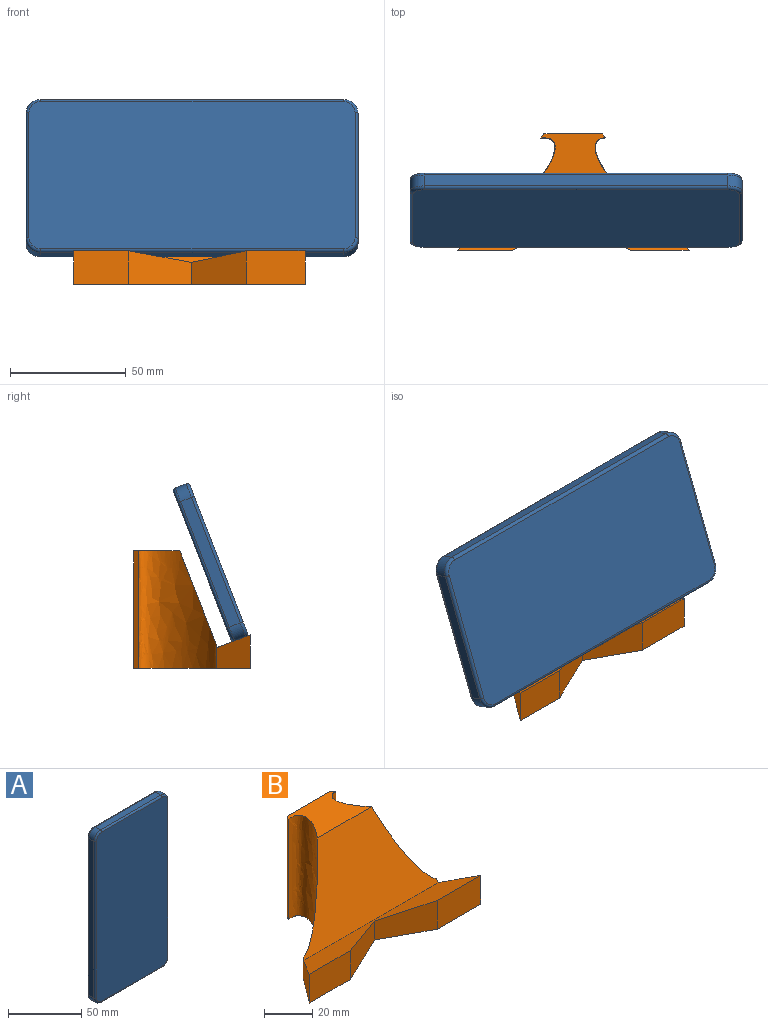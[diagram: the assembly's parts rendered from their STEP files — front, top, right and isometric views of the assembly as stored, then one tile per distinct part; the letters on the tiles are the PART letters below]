
ASSEMBLY  parts=2 mates=1
PART A: 26 faces, bbox 71.9x7.6x144.6 mm
  f0: plane 58.17x5.08mm, normal (0,0,-1), area 295.5mm2, adj f1,f7,f14,f22
  f1: cylinder r=6.35mm len=6.35mm, axis (0,1,0), area 50.7mm2, adj f0,f2,f12,f20
  f2: plane 130.81x5.08mm, normal (1,0,0), area 664.5mm2, adj f1,f3,f10,f18
  f3: cylinder r=6.35mm len=6.35mm, axis (0,1,0), area 50.7mm2, adj f2,f4,f11,f19
  f4: plane 58.17x5.08mm, normal (0,0,1), area 295.5mm2, adj f3,f5,f13,f21
  f5: cylinder r=6.35mm len=6.35mm, axis (0,1,0), area 50.7mm2, adj f4,f6,f15,f23
  f6: plane 130.81x5.08mm, normal (-1,0,0), area 664.5mm2, adj f5,f7,f17,f25
  f7: cylinder r=6.35mm len=6.35mm, axis (0,1,0), area 50.7mm2, adj f0,f6,f16,f24
  f8: plane 140.97x68.33mm, normal (0,-1,0), area 9609.8mm2, adj f18,f19,f20,f21,f22,f23,f24,f25
  f9: plane 140.97x68.33mm, normal (0,1,0), area 9609.8mm2, adj f10,f11,f12,f13,f14,f15,f16,f17
  f10: cylinder r=1.27mm len=130.81mm, axis (0,0,1), area 261mm2, adj f2,f9,f11,f12
  f11: torus R=5.08mm, axis (0,-1,0), area 18.5mm2, adj f3,f9,f10,f13
  f12: torus R=5.08mm, axis (0,-1,0), area 18.5mm2, adj f1,f9,f10,f14
  f13: cylinder r=1.27mm len=58.17mm, axis (-1,0,0), area 116mm2, adj f4,f9,f11,f15
  f14: cylinder r=1.27mm len=58.17mm, axis (1,0,0), area 116mm2, adj f0,f9,f12,f16
  f15: torus R=5.08mm, axis (0,-1,0), area 18.5mm2, adj f5,f9,f13,f17
  f16: torus R=5.08mm, axis (0,-1,0), area 18.5mm2, adj f7,f9,f14,f17
  f17: cylinder r=1.27mm len=130.81mm, axis (0,0,-1), area 261mm2, adj f6,f9,f15,f16
  f18: cylinder r=1.27mm len=130.81mm, axis (0,0,-1), area 261mm2, adj f2,f8,f19,f20
  f19: torus R=5.08mm, axis (0,-1,0), area 18.5mm2, adj f3,f8,f18,f21
  f20: torus R=5.08mm, axis (0,-1,0), area 18.5mm2, adj f1,f8,f18,f22
  f21: cylinder r=1.27mm len=58.17mm, axis (1,0,0), area 116mm2, adj f4,f8,f19,f23
  f22: cylinder r=1.27mm len=58.17mm, axis (-1,0,0), area 116mm2, adj f0,f8,f20,f24
  f23: torus R=5.08mm, axis (0,-1,0), area 18.5mm2, adj f5,f8,f21,f25
  f24: torus R=5.08mm, axis (0,-1,0), area 18.5mm2, adj f7,f8,f22,f25
  f25: cylinder r=1.27mm len=130.81mm, axis (0,0,1), area 261mm2, adj f6,f8,f23,f24
PART B: 15 faces, bbox 100.1x50.2x50.8 mm
  f0: plane 50.8x1.83mm, normal (-0.8,0.6,0), area 116mm2, adj f4,f10,f11,f14
  f1: plane 14.57x14.53mm, normal (-0.8,0.6,0), area 212.8mm2, adj f4,f5,f6,f12,f14
  f2: plane 14.84x14.57mm, normal (0.8,0.6,0), area 216.9mm2, adj f4,f5,f7,f12,f13
  f3: plane 50.8x1.73mm, normal (0.8,0.6,0), area 109.3mm2, adj f4,f10,f11,f13
  f4: plane 100.06x50.23mm, normal (0,0,-1), area 2200.9mm2, adj f0,f1,f2,f3,f6,f7,f8,f9
  f5: plane 79.04x41.73mm, normal (0,-0.93,0.36), area 2270.8mm2, adj f1,f2,f10,f12,f13,f14
  f6: plane 23.86x14.57mm, normal (0,-1,0), area 347.6mm2, adj f1,f4,f8,f12
  f7: plane 25.4x14.57mm, normal (0,-1,0), area 370mm2, adj f2,f4,f9,f12
  f8: plane 26.95x14.57mm, normal (0.43,-0.9,0), area 360.3mm2, adj f4,f6,f9,f12
  f9: plane 23.85x14.57mm, normal (-0.48,-0.88,0), area 327mm2, adj f4,f7,f8,f12
  f10: plane 31.54x19.86mm, normal (0,0,1), area 439.5mm2, adj f0,f3,f5,f11,f13,f14
  f11: plane 50.8x25.4mm, normal (0,1,0), area 1290.3mm2, adj f0,f3,f4,f10
  f12: plane 100.06x14.14mm, normal (0,0.36,0.93), area 1006.5mm2, adj f1,f2,f5,f6,f7,f8,f9
  f13: extruded ~50.8x33.66mm, area 1944.1mm2, adj f2,f3,f4,f5,f10
  f14: extruded ~50.8x33.98mm, area 2045.9mm2, adj f0,f1,f4,f5,f10
PLACE A rot(axis=(0.7,0.13,0.7),165deg) t=(-71.74,5.74,55.71)mm
PLACE B t=(-0.35,-20.71,-24.6)mm fixed
MATE planar A.f6 <-> B.f12  axis (0,-0.36,-0.93) through (0.02,-16.4,-11.71)mm
